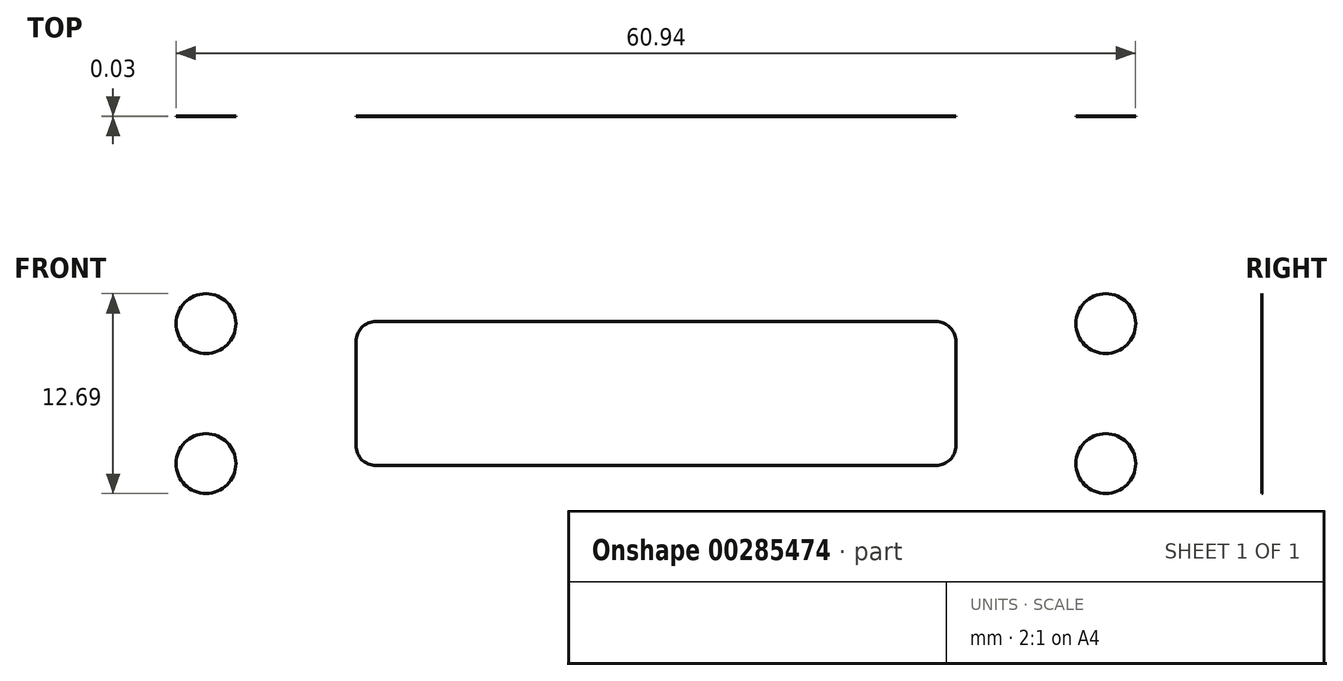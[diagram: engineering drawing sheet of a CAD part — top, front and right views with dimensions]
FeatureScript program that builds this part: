
annotation { "Feature Type Name" : "Feature", "Feature Type Description" : "" }
export const myFeature = defineFeature(function(context is Context, id is Id, definition is map)
    precondition{}
    {
        {
            var Q0;
            Q0=qCreatedBy(makeId("Front.planeOp"),FACE);
            var sketch = newSketch(context, id + "F0", { "sketchPlane" : qUnion([Q0])});
            skLineSegment(sketch, "E0.bottom", {"start": v(1.27, 0) * mm, "end": v(36.83, 0) * mm});
            skLineSegment(sketch, "E0.top", {"start": v(1.27, 9.14) * mm, "end": v(36.83, 9.14) * mm});
            skLineSegment(sketch, "E0.left", {"start": v(0, 1.27) * mm, "end": v(0, 7.87) * mm});
            skLineSegment(sketch, "E0.right", {"start": v(38.1, 1.27) * mm, "end": v(38.1, 7.87) * mm});
            skCircle(sketch, "E1", {"center": v(-9.53, 9.02) * mm, "radius": 1.9 * mm});
            skCircle(sketch, "E2", {"center": v(-9.53, 0.13) * mm, "radius": 1.9 * mm});
            skCircle(sketch, "E3", {"center": v(47.63, 9.02) * mm, "radius": 1.9 * mm});
            skCircle(sketch, "E4", {"center": v(47.63, 0.13) * mm, "radius": 1.9 * mm});
            skLineSegment(sketch, "E5", {"start": v(0, 4.57) * mm, "end": v(-9.53, 4.57) * mm, "construction": true});
            skLineSegment(sketch, "E6", {"start": v(-9.53, 9.02) * mm, "end": v(-9.53, 0.13) * mm, "construction": true});
            skLineSegment(sketch, "E7", {"start": v(47.63, 9.02) * mm, "end": v(47.63, 0.13) * mm, "construction": true});
            skLineSegment(sketch, "E8", {"start": v(38.1, 4.57) * mm, "end": v(47.63, 4.57) * mm, "construction": true});
            skPoint(sketch, "E8.endSnap0", {"position": v(38.1, 4.57) * mm});
            skPoint(sketch, "E9.visualSharp", {"position": v(0, 9.14) * mm});
            skArc(sketch, "E9.filletArc", {"start": v(1.27, 9.14) * mm, "mid": v(0.37, 8.77) * mm, "end": v(0, 7.87) * mm});
            skPoint(sketch, "E10.visualSharp", {"position": v(38.1, 9.14) * mm});
            skArc(sketch, "E10.filletArc", {"start": v(38.1, 7.87) * mm, "mid": v(37.73, 8.77) * mm, "end": v(36.83, 9.14) * mm});
            skPoint(sketch, "E11.visualSharp", {"position": v(38.1, 0) * mm});
            skArc(sketch, "E11.filletArc", {"start": v(36.83, 0) * mm, "mid": v(37.73, 0.37) * mm, "end": v(38.1, 1.27) * mm});
            skPoint(sketch, "E12.visualSharp", {"position": v(0, 0) * mm});
            skArc(sketch, "E12.filletArc", {"start": v(0, 1.27) * mm, "mid": v(0.37, 0.37) * mm, "end": v(1.27, 0) * mm});
            skLineSegment(sketch, "E13", {"start": v(19.05, 9.14) * mm, "end": v(19.05, 0) * mm, "construction": true});
            skSolve(sketch);
        }
        {
            var Q0;
            Q0=qSketchRegion(id+"F0",true);
            extrude(context, id + "F1", {"entities" : qUnion([Q0]), "depth" : 0.03 * mm});
        }
    });
